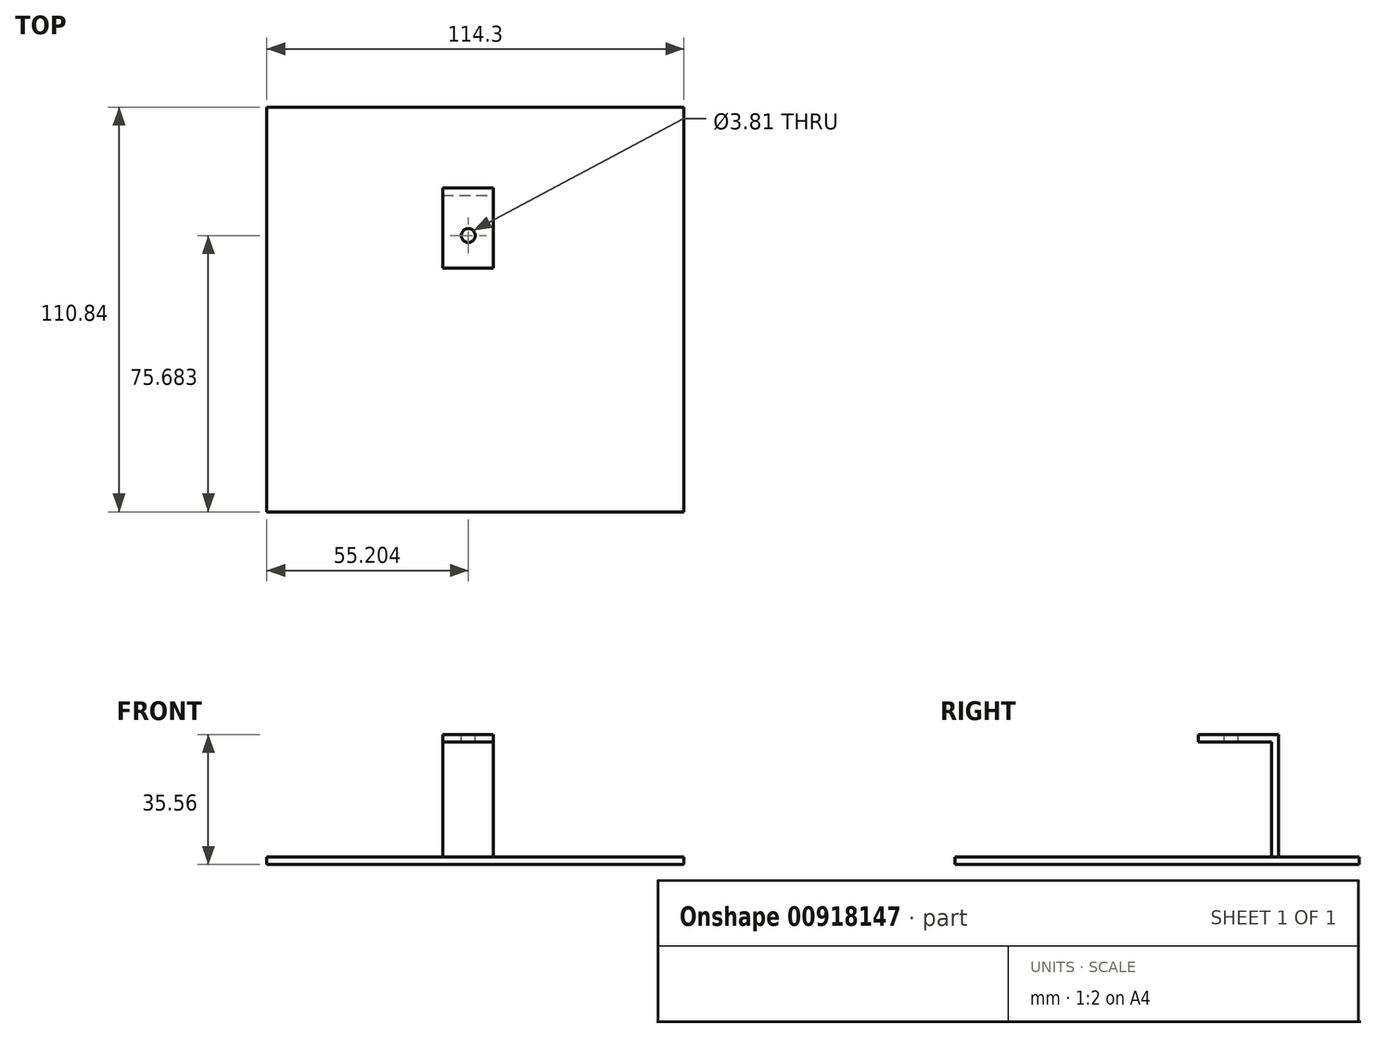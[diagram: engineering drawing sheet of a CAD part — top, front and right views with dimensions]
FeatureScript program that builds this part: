
annotation { "Feature Type Name" : "Feature", "Feature Type Description" : "" }
export const myFeature = defineFeature(function(context is Context, id is Id, definition is map)
    precondition{}
    {
        {
            var Q0;
            Q0=qCreatedBy(makeId("Top.planeOp"),FACE);
            var sketch = newSketch(context, id + "F0", { "sketchPlane" : qUnion([Q0])});
            skLineSegment(sketch, "E0.bottom", {"start": v(57.15, -55.42) * mm, "end": v(-57.15, -55.42) * mm});
            skLineSegment(sketch, "E0.top", {"start": v(57.15, 55.42) * mm, "end": v(-57.15, 55.42) * mm});
            skLineSegment(sketch, "E0.left", {"start": v(57.15, -55.42) * mm, "end": v(57.15, 55.42) * mm});
            skLineSegment(sketch, "E0.right", {"start": v(-57.15, -55.42) * mm, "end": v(-57.15, 55.42) * mm});
            skPoint(sketch, "E0.middle", {"position": v(0, 0) * mm});
            skLineSegment(sketch, "E1", {"start": v(-8.97, 33.33) * mm, "end": v(4.9, 33.33) * mm});
            skPoint(sketch, "E2", {"position": v(-8.97, 33.33) * mm});
            skPoint(sketch, "E3", {"position": v(4.9, 33.33) * mm});
            skSolve(sketch);
        }
        {
            var Q0;
            Q0=sQuery(id+"F0.wireOp",EDGE,"E1");
            extrude(context, id + "F1", {"bodyType" : ToolBodyType.SURFACE, "surfaceEntities" : qUnion([Q0]), "depth" : 35.56 * mm, "offsetDistance" : 25.4 * mm});
        }
        {
            var Q0;
            Q0 = qSketchRegion(id + "F0", true);
            extrude(context, id + "F2", {"entities" : qUnion([Q0]), "depth" : 2 * mm, "offsetDistance" : 25.4 * mm});
        }
        {
            var Q0;
            Q0=makeQuery(id+"F1.opExtrude","SWEPT_FACE",FACE,{"disambiguationData":[OSD([sQuery(id+"F0.wireOp",EDGE,"E1")])]});
            extrude(context, id + "F3", {"entities" : qUnion([Q0]), "operationType" : NewBodyOperationType.ADD, "depth" : 2 * mm, "offsetDistance" : 25.4 * mm});
        }
        {
            var Q0;
            Q0=makeQuery(id+"F3.opExtrude","CAP_FACE",FACE,{"disambiguationData":[OSD([sQuery(id+"F0.wireOp",EDGE,"E1")])],"isStart":false});
            var sketch = newSketch(context, id + "F4", { "sketchPlane" : qUnion([Q0])});
            skLineSegment(sketch, "E4", {"start": v(-8.97, 35.56) * mm, "end": v(4.9, 35.56) * mm});
            skSolve(sketch);
        }
        {
            var Q0;
            Q0=sQuery(id+"F4.wireOp",EDGE,"E4");
            extrude(context, id + "F5", {"bodyType" : ToolBodyType.SURFACE, "surfaceEntities" : qUnion([Q0]), "depth" : 20 * mm, "offsetDistance" : 25.4 * mm});
        }
        {
            var Q0;
            Q0=makeQuery(id+"F5.opExtrude","SWEPT_FACE",FACE,{"disambiguationData":[OSD([sQuery(id+"F4.wireOp",EDGE,"E4")])]});
            extrude(context, id + "F6", {"entities" : qUnion([Q0]), "operationType" : NewBodyOperationType.ADD, "depth" : 2 * mm, "offsetDistance" : 25.4 * mm});
        }
        {
            var Q0;
            Q0=makeQuery(id+"F5.opExtrude","SWEPT_FACE",FACE,{"disambiguationData":[OSD([sQuery(id+"F4.wireOp",EDGE,"E4")])]});
            var sketch = newSketch(context, id + "F7", { "sketchPlane" : qUnion([Q0])});
            skCircle(sketch, "E5", {"center": v(-1.95, -20.26) * mm, "radius": 1.9 * mm});
            skSolve(sketch);
        }
        {
            var Q0;
            Q0=makeQuery(id+"F7.imprint","IMPRINT",FACE,{"disambiguationData":[TD([[makeQuery(id+"F7.imprint","IMPRINT",EDGE,{"derivedFrom":sQuery(id+"F7.wireOp",EDGE,"E5")}),1.0]])]});
            extrude(context, id + "F8", {"entities" : qUnion([Q0]), "operationType" : NewBodyOperationType.REMOVE, "depth" : 6.86 * mm, "offsetDistance" : 25.4 * mm, "hasSecondDirection" : true, "secondDirectionOppositeDirection" : true, "secondDirectionDepth" : 2.03 * mm});
        }
    });
